# Revit family: xFaucet_Lavatory-Two_Handle-American_Standard-Monterrey-6540.173
name_source: partatom
category: Plumbing Fixtures
revit_build: Autodesk Revit 2014 (Build: 20130308_1515(x64)
units: mm (PartAtom-declared; Revit-internal decimal feet)

## types (1)
- 6540.173
    ADA Compliant = Yes
    Assembly Code = D2020
    CW Connection = Yes
    CWFU = 1.5
    Cold Water Connection Diameter = 1/2"
    Cold Water Connection Radius = 1/4"
    Cold Water Connection Width = 4"
    Default Elevation = 0"
    Description = Monterrey Two-Handle 8" Widespread Lavatory Faucet, Rigid/Swivel Gooseneck Spout and Third Water Inlet.
    Flow Rate = 1.5 gpm (5.7 L/min)
    HW Connection = Yes
    HWFU = 1.5
    Height = 10 5/8"
    Hot Water Connection Diameter = 1"
    Hot Water Connection Radius = 1/4"
    Hot Water Connection Width = 4"
    IAPMO Compliance = Lead Free
    Installation Type = Deck Mounted
    Length = 5"
    Manufacturer = American Standard
    Material = Brass-American Standard-002-Polished Chrome
    Model = 6540.173
    Price = Prices may vary. Please consult Manufacturer Representative for most up-to-date price list.
    Product Page URL = http://www.americanstandard-us.com
    Specification = Two-handle widespread lavatory faucet shall feature cast brass valve bodies with 8" rigid copper connection and third water inlet. Shall feature water-conserving 1.5 gpm/5.7 L/min. pressure compensating aerator. Vandal-Resistant handles. Shall also feature 1/4 turn washerless ceramic disc valve cartridges. Field-convertible rigid/swivel spout. Fitting shall be American Standard Model # 6540.173.002.
    URL = http://www.americanstandard-us.com
    Vent Connection = No
    WFU = 0
    Warranty Information = Limited Lifetime Warranty
    Waste Connection = No
    Width = 15 3/4"

## geometry (parser evidence)
native form markers: Sweep x1
no freeform markers — native parametric forms only
